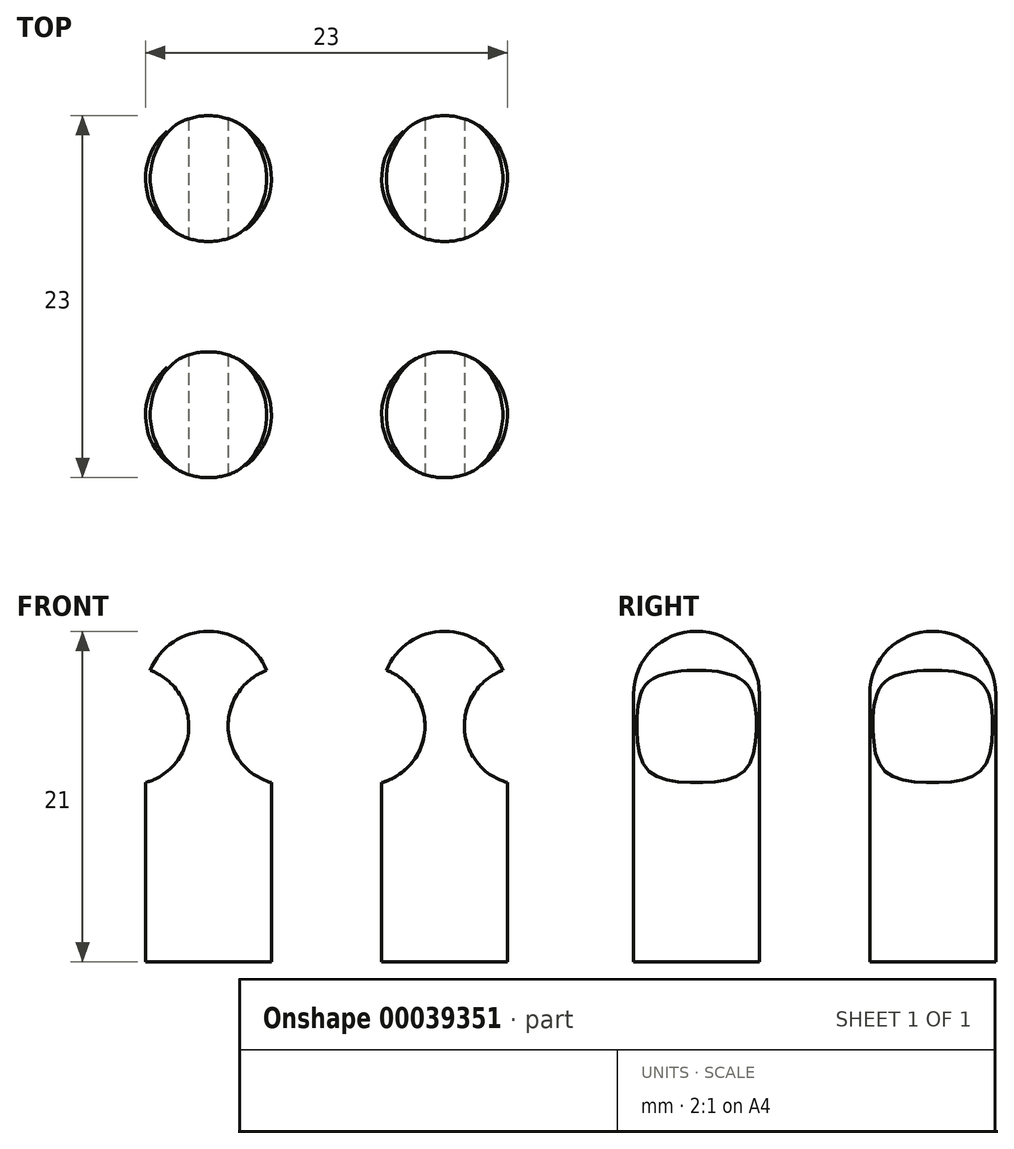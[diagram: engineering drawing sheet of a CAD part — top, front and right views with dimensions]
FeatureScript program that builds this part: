
annotation { "Feature Type Name" : "Feature", "Feature Type Description" : "" }
export const myFeature = defineFeature(function(context is Context, id is Id, definition is map)
    precondition{}
    {
        {
            var Q0;
            Q0=qCreatedBy(makeId("Top.planeOp"),FACE);
            var sketch = newSketch(context, id + "F0", { "sketchPlane" : qUnion([Q0])});
            skCircle(sketch, "E0", {"center": v(0, 0) * mm, "radius": 4 * mm});
            skSolve(sketch);
        }
        {
            var Q0;
            Q0=qSketchRegion(id+"F0",true);
            extrude(context, id + "F1", {"entities" : qUnion([Q0]), "depth" : 17 * mm});
        }
        {
            var Q0;
            Q0=makeQuery(id+"F1.opExtrude","CAP_FACE",FACE,{"disambiguationData":[OSD([sQuery(id+"F0.wireOp",EDGE,"E0")])],"isStart":false});
            var sketch = newSketch(context, id + "F2", { "sketchPlane" : qUnion([Q0])});
            skArc(sketch, "E1", {"start": v(0, -4) * mm, "mid": v(4, 0) * mm, "end": v(0, 4) * mm});
            skLineSegment(sketch, "E2", {"start": v(0, 4) * mm, "end": v(0, -4) * mm});
            skSolve(sketch);
        }
        {
            var Q0;
            Q0=qSketchRegion(id+"F2",true);
            var Q1;
            Q1=sQuery(id+"F2.wireOp",EDGE,"E2");
            revolve(context, id + "F3", {"operationType" : NewBodyOperationType.ADD, "entities" : qUnion([Q0]), "axis" : qUnion([Q1]), "revolveType" : RevolveType.ONE_DIRECTION, "angle" : 180 * degree});
        }
        {
            var Q0;
            Q0=qCreatedBy(makeId("Front.planeOp"),FACE);
            var sketch = newSketch(context, id + "F4", { "sketchPlane" : qUnion([Q0])});
            skLineSegment(sketch, "E3", {"start": v(0, 0) * mm, "end": v(0, 15) * mm, "construction": true});
            skLineSegment(sketch, "E4", {"start": v(-5, 15) * mm, "end": v(5, 15) * mm, "construction": true});
            skCircle(sketch, "E5", {"center": v(-5, 15) * mm, "radius": 3.75 * mm});
            skCircle(sketch, "E6.MirrorC", {"center": v(5, 15) * mm, "radius": 3.75 * mm});
            skSolve(sketch);
        }
        {
            var Q0;
            Q0 = qSketchRegion(id + "F4", true);
            extrude(context, id + "F5", {"entities" : qUnion([Q0]), "operationType" : NewBodyOperationType.REMOVE, "endBound" : BoundingType.THROUGH_ALL, "oppositeDirection" : true, "depth" : 25 * mm, "hasSecondDirection" : true, "secondDirectionBound" : SecondDirectionBoundingType.THROUGH_ALL, "secondDirectionOppositeDirection" : false, "secondDirectionDepth" : 25 * mm});
        }
        {
            var Q0;
            Q0=makeQuery(id+"F1.opExtrude","SWEPT_BODY",BODY,{"disambiguationData":[OSD([sQuery(id+"F0.wireOp",EDGE,"E0")])]});
            transform(context, id + "F6", {"entities" : qUnion([Q0]), "transformType" : TransformType.TRANSLATION_3D, "dx" : 15 * mm, "dy" : 0 * mm, "dz" : 0 * mm, "makeCopy" : true});
        }
        {
            var Q0;
            Q0=makeQuery(id+"F1.opExtrude","SWEPT_BODY",BODY,{"disambiguationData":[OSD([sQuery(id+"F0.wireOp",EDGE,"E0")])]});
            var Q1;
            Q1=makeQuery(id+"F6.opPattern","COPY",BODY,{"derivedFrom":makeQuery(id+"F1.opExtrude","SWEPT_BODY",BODY,{"disambiguationData":[OSD([sQuery(id+"F0.wireOp",EDGE,"E0")])]}),"instanceName":"1"});
            transform(context, id + "F7", {"entities" : qUnion([Q0, Q1]), "transformType" : TransformType.TRANSLATION_3D, "dx" : 0 * mm, "dy" : 15 * mm, "dz" : 0 * mm, "makeCopy" : true});
        }
    });
